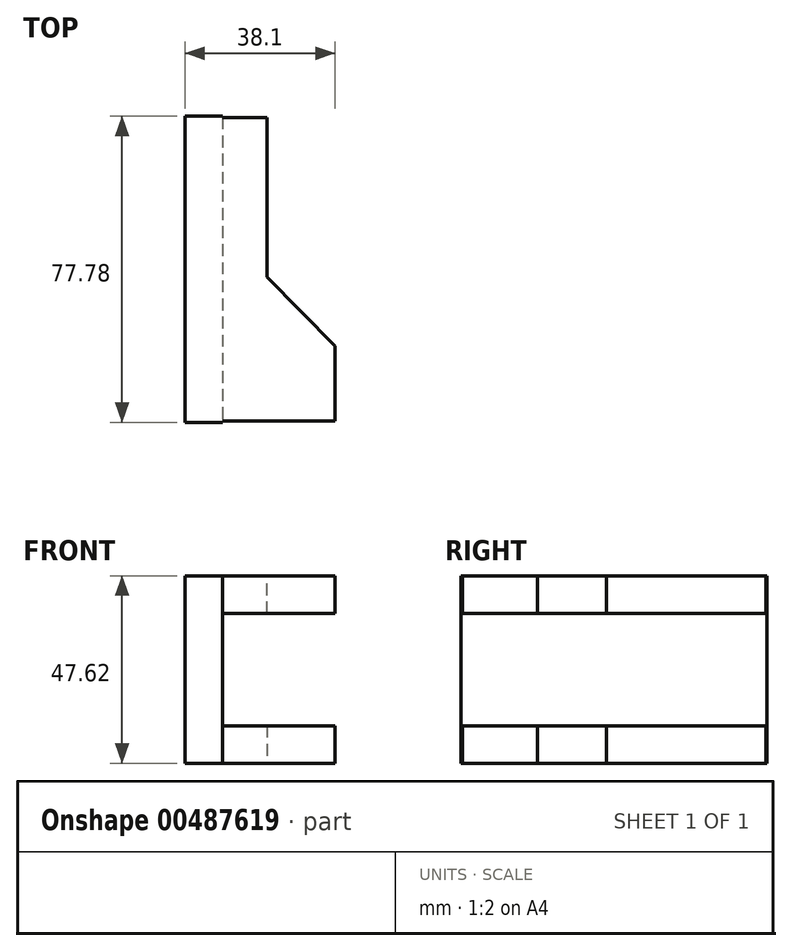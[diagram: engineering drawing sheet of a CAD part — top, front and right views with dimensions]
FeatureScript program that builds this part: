
annotation { "Feature Type Name" : "Feature", "Feature Type Description" : "" }
export const myFeature = defineFeature(function(context is Context, id is Id, definition is map)
    precondition{}
    {
        {
            var Q0;
            Q0=qCreatedBy(makeId("Right.planeOp"),FACE);
            var sketch = newSketch(context, id + "F0", { "sketchPlane" : qUnion([Q0])});
            skLineSegment(sketch, "E0.bottom", {"start": v(38.9, 23.81) * mm, "end": v(-38.9, 23.81) * mm});
            skLineSegment(sketch, "E0.top", {"start": v(38.9, -23.81) * mm, "end": v(-38.9, -23.81) * mm});
            skLineSegment(sketch, "E0.left", {"start": v(38.9, 23.81) * mm, "end": v(38.9, -23.81) * mm});
            skLineSegment(sketch, "E0.right", {"start": v(-38.9, 23.81) * mm, "end": v(-38.9, -23.81) * mm});
            skPoint(sketch, "E0.middle", {"position": v(0, 0) * mm});
            skSolve(sketch);
        }
        {
            var Q0;
            Q0=makeQuery(id+"F0.imprint","IMPRINT",FACE,{"disambiguationData":[TD([[makeQuery(id+"F0.imprint","IMPRINT",EDGE,{"derivedFrom":sQuery(id+"F0.wireOp",EDGE,"E0.bottom")}),1.0]])]});
            extrude(context, id + "F1", {"entities" : qUnion([Q0]), "depth" : 9.52 * mm});
        }
        {
            var Q0;
            Q0=qCreatedBy(makeId("Right.planeOp"),FACE);
            var sketch = newSketch(context, id + "F2", { "sketchPlane" : qUnion([Q0])});
            skCircle(sketch, "E1", {"center": v(0, 0) * mm, "radius": 12.64 * mm});
            skSolve(sketch);
        }
        {
            var Q0;
            Q0 = qSketchRegion(id + "F2", true);
            extrude(context, id + "F3", {"entities" : qUnion([Q0]), "operationType" : NewBodyOperationType.REMOVE, "endBound" : BoundingType.THROUGH_ALL, "oppositeDirection" : true, "depth" : 25.4 * mm});
        }
        {
            var Q0;
            Q0=makeQuery(id+"F1.opExtrude","SWEPT_FACE",FACE,{"disambiguationData":[OSD([sQuery(id+"F0.wireOp",EDGE,"E0.bottom")])]});
            var sketch = newSketch(context, id + "F4", { "sketchPlane" : qUnion([Q0])});
            skLineSegment(sketch, "E2", {"start": v(0, -38.57) * mm, "end": v(38.1, -38.57) * mm});
            skLineSegment(sketch, "E3", {"start": v(38.1, -38.57) * mm, "end": v(38.1, -19.52) * mm});
            skLineSegment(sketch, "E4", {"start": v(38.1, -19.52) * mm, "end": v(20.83, -1.96) * mm});
            skLineSegment(sketch, "E5", {"start": v(20.83, -1.96) * mm, "end": v(20.83, 38.57) * mm});
            skLineSegment(sketch, "E6", {"start": v(20.83, 38.57) * mm, "end": v(0, 38.57) * mm});
            skLineSegment(sketch, "E7", {"start": v(0, -38.57) * mm, "end": v(0, 38.57) * mm});
            skSolve(sketch);
        }
        {
            var Q0;
            Q0 = qSketchRegion(id + "F4", true);
            extrude(context, id + "F5", {"entities" : qUnion([Q0]), "oppositeDirection" : true, "depth" : 9.52 * mm});
        }
        {
            var Q0;
            Q0=makeQuery(id+"F5.opExtrude","SWEPT_BODY",BODY,{"disambiguationData":[OSD([sQuery(id+"F4.wireOp",EDGE,"E2"),sQuery(id+"F4.wireOp",EDGE,"E3"),sQuery(id+"F4.wireOp",EDGE,"E4"),sQuery(id+"F4.wireOp",EDGE,"E5"),sQuery(id+"F4.wireOp",EDGE,"E6"),sQuery(id+"F4.wireOp",EDGE,"E7")])]});
            var Q1;
            Q1=qCreatedBy(makeId("Top.planeOp"),FACE);
            mirror(context, id + "F6", {"operationType" : NewBodyOperationType.ADD, "entities" : qUnion([Q0]), "mirrorPlane" : qUnion([Q1])});
        }
    });
